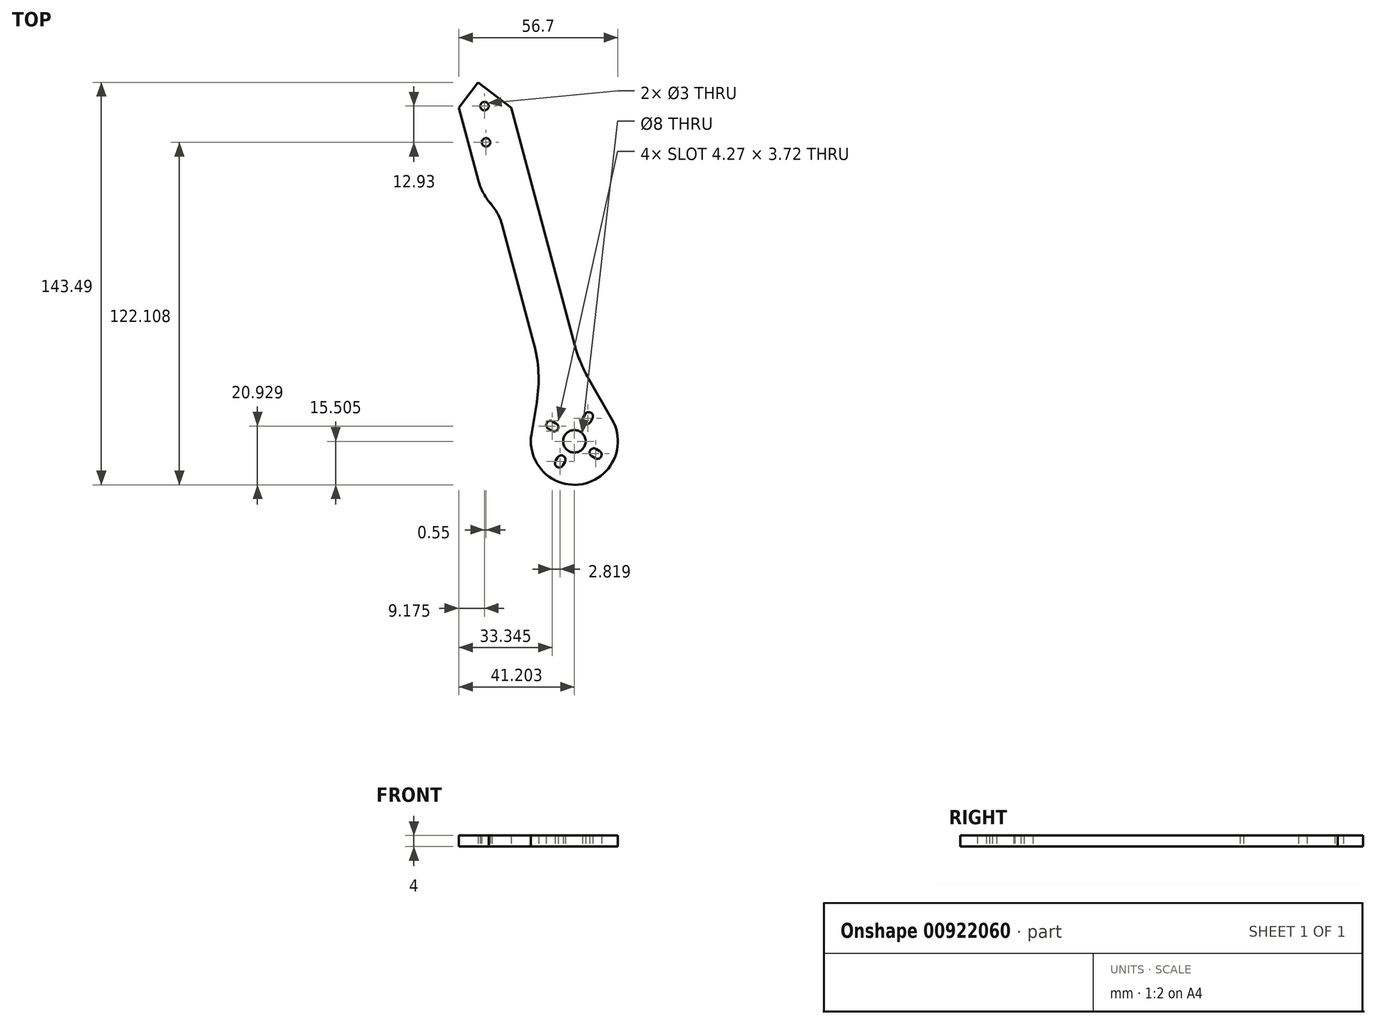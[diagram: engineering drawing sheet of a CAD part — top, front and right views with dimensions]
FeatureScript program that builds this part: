
annotation { "Feature Type Name" : "Feature", "Feature Type Description" : "" }
export const myFeature = defineFeature(function(context is Context, id is Id, definition is map)
    precondition{}
    {
        {
            var Q0;
            Q0=qCreatedBy(makeId("Top.planeOp"),FACE);
            var sketch = newSketch(context, id + "F0", { "sketchPlane" : qUnion([Q0])});
            skCircle(sketch, "E0", {"center": v(0, 0) * mm, "radius": 4 * mm});
            skLineSegment(sketch, "E1", {"start": v(0, 0) * mm, "end": v(6.19, 6.19) * mm});
            skLineSegment(sketch, "E2.bottom", {"start": v(7.78, 7.78) * mm, "end": v(7.78, 7.78) * mm});
            skLineSegment(sketch, "E2.top", {"start": v(4.6, 4.6) * mm, "end": v(4.6, 4.6) * mm});
            skLineSegment(sketch, "E2.left", {"start": v(7.78, 5.66) * mm, "end": v(6.72, 4.6) * mm});
            skLineSegment(sketch, "E2.right", {"start": v(5.66, 7.78) * mm, "end": v(4.6, 6.72) * mm});
            skPoint(sketch, "E2.middle", {"position": v(6.19, 6.19) * mm});
            skPoint(sketch, "E3.1.0", {"position": v(-6.73, 6.73) * mm});
            skLineSegment(sketch, "E3.1.1", {"start": v(-5.14, 5.14) * mm, "end": v(-5.14, 5.14) * mm});
            skLineSegment(sketch, "E3.1.2", {"start": v(-6.2, 8.32) * mm, "end": v(-5.14, 7.26) * mm});
            skLineSegment(sketch, "E3.1.3", {"start": v(-8.32, 6.2) * mm, "end": v(-7.26, 5.14) * mm});
            skLineSegment(sketch, "E3.1.4", {"start": v(-8.32, 8.32) * mm, "end": v(-8.32, 8.32) * mm});
            skPoint(sketch, "E3.2.0", {"position": v(-7.27, -6.19) * mm});
            skLineSegment(sketch, "E3.2.1", {"start": v(-5.68, -4.6) * mm, "end": v(-5.68, -4.6) * mm});
            skLineSegment(sketch, "E3.2.2", {"start": v(-8.86, -5.66) * mm, "end": v(-7.8, -4.6) * mm});
            skLineSegment(sketch, "E3.2.3", {"start": v(-6.74, -7.78) * mm, "end": v(-5.68, -6.72) * mm});
            skLineSegment(sketch, "E3.2.4", {"start": v(-8.86, -7.78) * mm, "end": v(-8.86, -7.78) * mm});
            skPoint(sketch, "E3.3.0", {"position": v(5.64, -6.73) * mm});
            skLineSegment(sketch, "E3.3.1", {"start": v(4.05, -5.14) * mm, "end": v(4.05, -5.14) * mm});
            skLineSegment(sketch, "E3.3.2", {"start": v(5.11, -8.32) * mm, "end": v(4.05, -7.26) * mm});
            skLineSegment(sketch, "E3.3.3", {"start": v(7.24, -6.2) * mm, "end": v(6.17, -5.14) * mm});
            skLineSegment(sketch, "E3.3.4", {"start": v(7.24, -8.32) * mm, "end": v(7.24, -8.32) * mm});
            skPoint(sketch, "E3.center", {"position": v(-0.54, 0) * mm});
            skPoint(sketch, "E4.visualSharp", {"position": v(-9.38, 7.26) * mm});
            skArc(sketch, "E4.filletArc", {"start": v(-8.32, 8.32) * mm, "mid": v(-8.76, 7.26) * mm, "end": v(-8.32, 6.2) * mm});
            skPoint(sketch, "E5.visualSharp", {"position": v(-7.26, 9.38) * mm});
            skArc(sketch, "E5.filletArc", {"start": v(-6.2, 8.32) * mm, "mid": v(-7.26, 8.76) * mm, "end": v(-8.32, 8.32) * mm});
            skPoint(sketch, "E6.visualSharp", {"position": v(-4.08, 6.2) * mm});
            skArc(sketch, "E6.filletArc", {"start": v(-5.14, 5.14) * mm, "mid": v(-4.7, 6.2) * mm, "end": v(-5.14, 7.26) * mm});
            skPoint(sketch, "E7.visualSharp", {"position": v(-6.2, 4.08) * mm});
            skArc(sketch, "E7.filletArc", {"start": v(-7.26, 5.14) * mm, "mid": v(-6.2, 4.7) * mm, "end": v(-5.14, 5.14) * mm});
            skPoint(sketch, "E8.visualSharp", {"position": v(6.72, 8.84) * mm});
            skArc(sketch, "E8.filletArc", {"start": v(7.78, 7.78) * mm, "mid": v(6.72, 8.22) * mm, "end": v(5.66, 7.78) * mm});
            skPoint(sketch, "E9.visualSharp", {"position": v(8.84, 6.72) * mm});
            skArc(sketch, "E9.filletArc", {"start": v(7.78, 5.66) * mm, "mid": v(8.22, 6.72) * mm, "end": v(7.78, 7.78) * mm});
            skPoint(sketch, "E10.visualSharp", {"position": v(5.66, 3.54) * mm});
            skArc(sketch, "E10.filletArc", {"start": v(4.6, 4.6) * mm, "mid": v(5.66, 4.16) * mm, "end": v(6.72, 4.6) * mm});
            skPoint(sketch, "E11.visualSharp", {"position": v(3.54, 5.66) * mm});
            skArc(sketch, "E11.filletArc", {"start": v(4.6, 6.72) * mm, "mid": v(4.16, 5.66) * mm, "end": v(4.6, 4.6) * mm});
            skPoint(sketch, "E12.visualSharp", {"position": v(5.11, -4.08) * mm});
            skArc(sketch, "E12.filletArc", {"start": v(6.17, -5.14) * mm, "mid": v(5.11, -4.7) * mm, "end": v(4.05, -5.14) * mm});
            skPoint(sketch, "E13.visualSharp", {"position": v(3, -6.2) * mm});
            skArc(sketch, "E13.filletArc", {"start": v(4.05, -5.14) * mm, "mid": v(3.61, -6.2) * mm, "end": v(4.05, -7.26) * mm});
            skPoint(sketch, "E14.visualSharp", {"position": v(6.17, -9.38) * mm});
            skArc(sketch, "E14.filletArc", {"start": v(5.11, -8.32) * mm, "mid": v(6.17, -8.76) * mm, "end": v(7.24, -8.32) * mm});
            skPoint(sketch, "E15.visualSharp", {"position": v(8.3, -7.26) * mm});
            skArc(sketch, "E15.filletArc", {"start": v(7.24, -8.32) * mm, "mid": v(7.67, -7.26) * mm, "end": v(7.24, -6.2) * mm});
            skPoint(sketch, "E16.visualSharp", {"position": v(-4.62, -5.66) * mm});
            skArc(sketch, "E16.filletArc", {"start": v(-5.68, -6.72) * mm, "mid": v(-5.24, -5.66) * mm, "end": v(-5.68, -4.6) * mm});
            skPoint(sketch, "E17.visualSharp", {"position": v(-6.74, -3.54) * mm});
            skArc(sketch, "E17.filletArc", {"start": v(-5.68, -4.6) * mm, "mid": v(-6.74, -4.16) * mm, "end": v(-7.8, -4.6) * mm});
            skPoint(sketch, "E18.visualSharp", {"position": v(-9.92, -6.72) * mm});
            skArc(sketch, "E18.filletArc", {"start": v(-8.86, -5.66) * mm, "mid": v(-9.3, -6.72) * mm, "end": v(-8.86, -7.78) * mm});
            skPoint(sketch, "E19.visualSharp", {"position": v(-7.8, -8.84) * mm});
            skArc(sketch, "E19.filletArc", {"start": v(-8.86, -7.78) * mm, "mid": v(-7.8, -8.22) * mm, "end": v(-6.74, -7.78) * mm});
            skLineSegment(sketch, "E20", {"start": v(0, 0) * mm, "end": v(-265, 0) * mm});
            skPoint(sketch, "E21.1.0", {"position": v(-270.66, -3.54) * mm});
            skPoint(sketch, "E21.1.1", {"position": v(-258.26, 3.54) * mm});
            skPoint(sketch, "E21.1.2", {"position": v(-255.08, 6.72) * mm});
            skCircle(sketch, "E21.1.3", {"center": v(-265, 0) * mm, "radius": 4 * mm});
            skPoint(sketch, "E21.1.4", {"position": v(-271.17, 9.38) * mm});
            skPoint(sketch, "E21.1.5", {"position": v(-257.2, 8.84) * mm});
            skPoint(sketch, "E21.1.6", {"position": v(-260.92, -6.2) * mm});
            skPoint(sketch, "E21.1.7", {"position": v(-270.11, 4.08) * mm});
            skPoint(sketch, "E21.1.8", {"position": v(-273.3, 7.26) * mm});
            skPoint(sketch, "E21.1.9", {"position": v(-268, 6.2) * mm});
            skPoint(sketch, "E21.1.10", {"position": v(-264.46, 0) * mm});
            skPoint(sketch, "E21.1.11", {"position": v(-271.72, -8.84) * mm});
            skPoint(sketch, "E21.1.12", {"position": v(-258.8, -4.08) * mm});
            skPoint(sketch, "E21.1.13", {"position": v(-273.84, -6.72) * mm});
            skPoint(sketch, "E21.1.14", {"position": v(-257.74, -9.38) * mm});
            skPoint(sketch, "E21.1.15", {"position": v(-268.54, -5.66) * mm});
            skPoint(sketch, "E21.1.16", {"position": v(-255.62, -7.26) * mm});
            skPoint(sketch, "E21.1.17", {"position": v(-260.38, 5.66) * mm});
            skPoint(sketch, "E21.1.18", {"position": v(-258.27, -6.73) * mm});
            skLineSegment(sketch, "E21.1.19", {"start": v(-265, 0) * mm, "end": v(-271.19, -6.19) * mm});
            skPoint(sketch, "E21.1.20", {"position": v(-271.19, -6.19) * mm});
            skPoint(sketch, "E21.1.21", {"position": v(-270.64, 6.73) * mm});
            skPoint(sketch, "E21.1.22", {"position": v(-257.73, 6.19) * mm});
            skArc(sketch, "E21.1.23", {"start": v(-271.17, 5.14) * mm, "mid": v(-270.11, 4.7) * mm, "end": v(-269.05, 5.14) * mm});
            skArc(sketch, "E21.1.24", {"start": v(-269.6, -6.72) * mm, "mid": v(-269.16, -5.66) * mm, "end": v(-269.6, -4.6) * mm});
            skArc(sketch, "E21.1.25", {"start": v(-269.6, -4.6) * mm, "mid": v(-270.66, -4.16) * mm, "end": v(-271.72, -4.6) * mm});
            skArc(sketch, "E21.1.26", {"start": v(-256.68, -8.32) * mm, "mid": v(-256.24, -7.26) * mm, "end": v(-256.68, -6.2) * mm});
            skArc(sketch, "E21.1.27", {"start": v(-258.8, -8.32) * mm, "mid": v(-257.74, -8.76) * mm, "end": v(-256.68, -8.32) * mm});
            skLineSegment(sketch, "E21.1.28", {"start": v(-258.8, -8.32) * mm, "end": v(-259.86, -7.26) * mm});
            skArc(sketch, "E21.1.29", {"start": v(-257.74, -5.14) * mm, "mid": v(-258.8, -4.7) * mm, "end": v(-259.86, -5.14) * mm});
            skArc(sketch, "E21.1.30", {"start": v(-259.86, -5.14) * mm, "mid": v(-260.3, -6.2) * mm, "end": v(-259.86, -7.26) * mm});
            skLineSegment(sketch, "E21.1.31", {"start": v(-256.68, -6.2) * mm, "end": v(-257.74, -5.14) * mm});
            skArc(sketch, "E21.1.32", {"start": v(-256.14, 7.78) * mm, "mid": v(-257.2, 8.22) * mm, "end": v(-258.26, 7.78) * mm});
            skLineSegment(sketch, "E21.1.33", {"start": v(-270.11, 8.32) * mm, "end": v(-269.05, 7.26) * mm});
            skArc(sketch, "E21.1.34", {"start": v(-272.78, -5.66) * mm, "mid": v(-273.22, -6.72) * mm, "end": v(-272.78, -7.78) * mm});
            skLineSegment(sketch, "E21.1.35", {"start": v(-272.24, 6.2) * mm, "end": v(-271.17, 5.14) * mm});
            skArc(sketch, "E21.1.36", {"start": v(-270.11, 8.32) * mm, "mid": v(-271.17, 8.76) * mm, "end": v(-272.24, 8.32) * mm});
            skArc(sketch, "E21.1.37", {"start": v(-259.32, 4.6) * mm, "mid": v(-258.26, 4.16) * mm, "end": v(-257.2, 4.6) * mm});
            skArc(sketch, "E21.1.38", {"start": v(-259.32, 6.72) * mm, "mid": v(-259.76, 5.66) * mm, "end": v(-259.32, 4.6) * mm});
            skLineSegment(sketch, "E21.1.39", {"start": v(-256.14, 5.66) * mm, "end": v(-257.2, 4.6) * mm});
            skArc(sketch, "E21.1.40", {"start": v(-269.05, 5.14) * mm, "mid": v(-268.61, 6.2) * mm, "end": v(-269.05, 7.26) * mm});
            skArc(sketch, "E21.1.41", {"start": v(-272.24, 8.32) * mm, "mid": v(-272.67, 7.26) * mm, "end": v(-272.24, 6.2) * mm});
            skArc(sketch, "E21.1.42", {"start": v(-256.14, 5.66) * mm, "mid": v(-255.7, 6.72) * mm, "end": v(-256.14, 7.78) * mm});
            skLineSegment(sketch, "E21.1.43", {"start": v(-258.26, 7.78) * mm, "end": v(-259.32, 6.72) * mm});
            skArc(sketch, "E21.1.44", {"start": v(-272.78, -7.78) * mm, "mid": v(-271.72, -8.22) * mm, "end": v(-270.66, -7.78) * mm});
            skLineSegment(sketch, "E21.1.45", {"start": v(-270.66, -7.78) * mm, "end": v(-269.6, -6.72) * mm});
            skLineSegment(sketch, "E21.1.46", {"start": v(-272.78, -5.66) * mm, "end": v(-271.72, -4.6) * mm});
            skPoint(sketch, "E21.center", {"position": v(-132.5, 0) * mm});
            skPoint(sketch, "E22.1.0", {"position": v(-161.58, 132.48) * mm});
            skPoint(sketch, "E22.1.1", {"position": v(-169.13, 120.94) * mm});
            skLineSegment(sketch, "E22.1.2", {"start": v(-166.8, 127.99) * mm, "end": v(-174.37, 132.36) * mm});
            skPoint(sketch, "E22.1.3", {"position": v(-174.37, 132.36) * mm});
            skPoint(sketch, "E22.1.4", {"position": v(-157.74, 120.14) * mm});
            skPoint(sketch, "E22.1.5", {"position": v(-166.65, 127.46) * mm});
            skPoint(sketch, "E22.1.6", {"position": v(-177.07, 132.19) * mm});
            skPoint(sketch, "E22.1.7", {"position": v(-156.24, 122.74) * mm});
            skPoint(sketch, "E22.1.8", {"position": v(-175.57, 134.78) * mm});
            skPoint(sketch, "E22.1.9", {"position": v(-160.13, 124.99) * mm});
            skPoint(sketch, "E22.1.10", {"position": v(-164.18, 133.98) * mm});
            skPoint(sketch, "E22.1.11", {"position": v(-158.93, 122.56) * mm});
            skPoint(sketch, "E22.1.12", {"position": v(-171.73, 122.44) * mm});
            skPoint(sketch, "E22.1.13", {"position": v(-161.63, 122.39) * mm});
            skPoint(sketch, "E22.1.14", {"position": v(-171.55, 119.74) * mm});
            skPoint(sketch, "E22.1.15", {"position": v(-173.98, 118.54) * mm});
            skPoint(sketch, "E22.1.16", {"position": v(-159.33, 136.38) * mm});
            skPoint(sketch, "E22.1.17", {"position": v(-161.93, 137.88) * mm});
            skCircle(sketch, "E22.1.18", {"center": v(-166.8, 127.99) * mm, "radius": 4 * mm});
            skPoint(sketch, "E22.1.19", {"position": v(-161.75, 135.18) * mm});
            skPoint(sketch, "E22.1.20", {"position": v(-171.67, 132.53) * mm});
            skPoint(sketch, "E22.1.21", {"position": v(-173.17, 129.94) * mm});
            skPoint(sketch, "E22.1.22", {"position": v(-171.38, 117.04) * mm});
            skArc(sketch, "E22.1.23", {"start": v(-156.99, 121.44) * mm, "mid": v(-156.84, 122.57) * mm, "end": v(-157.54, 123.49) * mm});
            skArc(sketch, "E22.1.24", {"start": v(-176.32, 133.49) * mm, "mid": v(-176.47, 132.35) * mm, "end": v(-175.77, 131.44) * mm});
            skArc(sketch, "E22.1.25", {"start": v(-174.47, 130.69) * mm, "mid": v(-173.33, 130.54) * mm, "end": v(-172.42, 131.24) * mm});
            skArc(sketch, "E22.1.26", {"start": v(-169.88, 119.64) * mm, "mid": v(-169.73, 120.78) * mm, "end": v(-170.43, 121.7) * mm});
            skArc(sketch, "E22.1.27", {"start": v(-172.42, 131.24) * mm, "mid": v(-172.27, 132.37) * mm, "end": v(-172.97, 133.28) * mm});
            skLineSegment(sketch, "E22.1.28", {"start": v(-174.27, 134.03) * mm, "end": v(-172.97, 133.28) * mm});
            skLineSegment(sketch, "E22.1.29", {"start": v(-170.63, 118.34) * mm, "end": v(-169.88, 119.64) * mm});
            skArc(sketch, "E22.1.30", {"start": v(-170.43, 121.7) * mm, "mid": v(-171.57, 121.84) * mm, "end": v(-172.48, 121.14) * mm});
            skLineSegment(sketch, "E22.1.31", {"start": v(-162.68, 136.58) * mm, "end": v(-163.43, 135.28) * mm});
            skLineSegment(sketch, "E22.1.32", {"start": v(-159.04, 120.89) * mm, "end": v(-160.33, 121.64) * mm});
            skLineSegment(sketch, "E22.1.33", {"start": v(-175.77, 131.44) * mm, "end": v(-174.47, 130.69) * mm});
            skArc(sketch, "E22.1.34", {"start": v(-160.63, 137.13) * mm, "mid": v(-161.77, 137.28) * mm, "end": v(-162.68, 136.58) * mm});
            skArc(sketch, "E22.1.35", {"start": v(-159.04, 120.89) * mm, "mid": v(-157.9, 120.74) * mm, "end": v(-156.99, 121.44) * mm});
            skLineSegment(sketch, "E22.1.36", {"start": v(-160.08, 135.08) * mm, "end": v(-160.83, 133.78) * mm});
            skArc(sketch, "E22.1.37", {"start": v(-172.68, 117.8) * mm, "mid": v(-171.54, 117.64) * mm, "end": v(-170.63, 118.34) * mm});
            skArc(sketch, "E22.1.38", {"start": v(-163.43, 135.28) * mm, "mid": v(-163.58, 134.14) * mm, "end": v(-162.88, 133.23) * mm});
            skArc(sketch, "E22.1.39", {"start": v(-162.88, 133.23) * mm, "mid": v(-161.74, 133.08) * mm, "end": v(-160.83, 133.78) * mm});
            skLineSegment(sketch, "E22.1.40", {"start": v(-173.23, 119.84) * mm, "end": v(-172.48, 121.14) * mm});
            skArc(sketch, "E22.1.41", {"start": v(-160.08, 135.08) * mm, "mid": v(-159.93, 136.22) * mm, "end": v(-160.63, 137.13) * mm});
            skArc(sketch, "E22.1.42", {"start": v(-158.83, 124.24) * mm, "mid": v(-159.97, 124.39) * mm, "end": v(-160.88, 123.69) * mm});
            skLineSegment(sketch, "E22.1.43", {"start": v(-157.54, 123.49) * mm, "end": v(-158.83, 124.24) * mm});
            skArc(sketch, "E22.1.44", {"start": v(-174.27, 134.03) * mm, "mid": v(-175.4, 134.18) * mm, "end": v(-176.32, 133.49) * mm});
            skArc(sketch, "E22.1.45", {"start": v(-173.23, 119.84) * mm, "mid": v(-173.38, 118.7) * mm, "end": v(-172.68, 117.8) * mm});
            skArc(sketch, "E22.1.46", {"start": v(-160.88, 123.69) * mm, "mid": v(-161.03, 122.55) * mm, "end": v(-160.33, 121.64) * mm});
            skLineSegment(sketch, "E22.anchor1", {"start": v(-132.5, 0) * mm, "end": v(-265, 0) * mm, "construction": true});
            skLineSegment(sketch, "E22.anchor2", {"start": v(-132.5, 0) * mm, "end": v(-166.8, 127.99) * mm, "construction": true});
            skPoint(sketch, "E23.1.0", {"position": v(-103.07, -137.88) * mm});
            skPoint(sketch, "E23.1.1", {"position": v(-90.63, -132.36) * mm});
            skPoint(sketch, "E23.1.2", {"position": v(-93.33, -132.53) * mm});
            skPoint(sketch, "E23.1.3", {"position": v(-108.76, -122.74) * mm});
            skPoint(sketch, "E23.1.4", {"position": v(-87.93, -132.19) * mm});
            skPoint(sketch, "E23.1.5", {"position": v(-103.25, -135.18) * mm});
            skPoint(sketch, "E23.1.6", {"position": v(-104.87, -124.99) * mm});
            skPoint(sketch, "E23.1.7", {"position": v(-103.37, -122.39) * mm});
            skPoint(sketch, "E23.1.8", {"position": v(-93.27, -122.44) * mm});
            skPoint(sketch, "E23.1.9", {"position": v(-95.87, -120.94) * mm});
            skPoint(sketch, "E23.1.10", {"position": v(-103.42, -132.48) * mm});
            skCircle(sketch, "E23.1.11", {"center": v(-98.2, -127.99) * mm, "radius": 4 * mm});
            skPoint(sketch, "E23.1.12", {"position": v(-106.07, -122.56) * mm});
            skPoint(sketch, "E23.1.13", {"position": v(-107.26, -120.14) * mm});
            skPoint(sketch, "E23.1.14", {"position": v(-93.45, -119.74) * mm});
            skLineSegment(sketch, "E23.1.15", {"start": v(-98.2, -127.99) * mm, "end": v(-90.63, -132.36) * mm});
            skPoint(sketch, "E23.1.16", {"position": v(-91.02, -118.54) * mm});
            skPoint(sketch, "E23.1.17", {"position": v(-93.62, -117.04) * mm});
            skPoint(sketch, "E23.1.18", {"position": v(-100.82, -133.98) * mm});
            skPoint(sketch, "E23.1.19", {"position": v(-105.67, -136.38) * mm});
            skPoint(sketch, "E23.1.20", {"position": v(-91.83, -129.94) * mm});
            skPoint(sketch, "E23.1.21", {"position": v(-98.35, -127.46) * mm});
            skPoint(sketch, "E23.1.22", {"position": v(-89.43, -134.78) * mm});
            skArc(sketch, "E23.1.23", {"start": v(-102.12, -133.23) * mm, "mid": v(-103.26, -133.08) * mm, "end": v(-104.17, -133.78) * mm});
            skArc(sketch, "E23.1.24", {"start": v(-92.58, -131.24) * mm, "mid": v(-92.73, -132.37) * mm, "end": v(-92.03, -133.28) * mm});
            skArc(sketch, "E23.1.25", {"start": v(-104.92, -135.08) * mm, "mid": v(-105.07, -136.22) * mm, "end": v(-104.37, -137.13) * mm});
            skArc(sketch, "E23.1.26", {"start": v(-106.17, -124.24) * mm, "mid": v(-105.03, -124.39) * mm, "end": v(-104.12, -123.69) * mm});
            skLineSegment(sketch, "E23.1.27", {"start": v(-107.46, -123.49) * mm, "end": v(-106.17, -124.24) * mm});
            skArc(sketch, "E23.1.28", {"start": v(-90.53, -130.69) * mm, "mid": v(-91.67, -130.54) * mm, "end": v(-92.58, -131.24) * mm});
            skArc(sketch, "E23.1.29", {"start": v(-101.57, -135.28) * mm, "mid": v(-101.42, -134.14) * mm, "end": v(-102.12, -133.23) * mm});
            skArc(sketch, "E23.1.30", {"start": v(-104.37, -137.13) * mm, "mid": v(-103.23, -137.28) * mm, "end": v(-102.32, -136.58) * mm});
            skLineSegment(sketch, "E23.1.31", {"start": v(-91.77, -119.84) * mm, "end": v(-92.52, -121.14) * mm});
            skArc(sketch, "E23.1.32", {"start": v(-105.96, -120.89) * mm, "mid": v(-107.1, -120.74) * mm, "end": v(-108.01, -121.44) * mm});
            skArc(sketch, "E23.1.33", {"start": v(-95.12, -119.64) * mm, "mid": v(-95.27, -120.78) * mm, "end": v(-94.57, -121.7) * mm});
            skLineSegment(sketch, "E23.1.34", {"start": v(-94.37, -118.34) * mm, "end": v(-95.12, -119.64) * mm});
            skLineSegment(sketch, "E23.1.35", {"start": v(-105.96, -120.89) * mm, "end": v(-104.67, -121.64) * mm});
            skArc(sketch, "E23.1.36", {"start": v(-91.77, -119.84) * mm, "mid": v(-91.62, -118.7) * mm, "end": v(-92.32, -117.8) * mm});
            skArc(sketch, "E23.1.37", {"start": v(-88.68, -133.49) * mm, "mid": v(-88.53, -132.35) * mm, "end": v(-89.23, -131.44) * mm});
            skArc(sketch, "E23.1.38", {"start": v(-90.73, -134.03) * mm, "mid": v(-89.6, -134.18) * mm, "end": v(-88.68, -133.49) * mm});
            skLineSegment(sketch, "E23.1.39", {"start": v(-104.92, -135.08) * mm, "end": v(-104.17, -133.78) * mm});
            skLineSegment(sketch, "E23.1.40", {"start": v(-89.23, -131.44) * mm, "end": v(-90.53, -130.69) * mm});
            skLineSegment(sketch, "E23.1.41", {"start": v(-102.32, -136.58) * mm, "end": v(-101.57, -135.28) * mm});
            skArc(sketch, "E23.1.42", {"start": v(-92.32, -117.8) * mm, "mid": v(-93.46, -117.64) * mm, "end": v(-94.37, -118.34) * mm});
            skArc(sketch, "E23.1.43", {"start": v(-108.01, -121.44) * mm, "mid": v(-108.16, -122.57) * mm, "end": v(-107.46, -123.49) * mm});
            skLineSegment(sketch, "E23.1.44", {"start": v(-90.73, -134.03) * mm, "end": v(-92.03, -133.28) * mm});
            skArc(sketch, "E23.1.45", {"start": v(-104.12, -123.69) * mm, "mid": v(-103.97, -122.55) * mm, "end": v(-104.67, -121.64) * mm});
            skArc(sketch, "E23.1.46", {"start": v(-94.57, -121.7) * mm, "mid": v(-93.43, -121.84) * mm, "end": v(-92.52, -121.14) * mm});
            skLineSegment(sketch, "E23.anchor1", {"start": v(-132.5, 0) * mm, "end": v(-166.65, 127.46) * mm, "construction": true});
            skLineSegment(sketch, "E23.anchor2", {"start": v(-132.5, 0) * mm, "end": v(-98.35, -127.46) * mm, "construction": true});
            skSolve(sketch);
        }
        {
            var Q0;
            Q0=qCreatedBy(makeId("Top.planeOp"),FACE);
            var sketch = newSketch(context, id + "F1", { "sketchPlane" : qUnion([Q0])});
            skCircle(sketch, "E24", {"center": v(-123.75, 0) * mm, "radius": 1.5 * mm});
            skCircle(sketch, "E25", {"center": v(-102.5, 0) * mm, "radius": 1.5 * mm});
            skLineSegment(sketch, "E26", {"start": v(-98.2, -127.99) * mm, "end": v(-166.8, 127.99) * mm});
            skLineSegment(sketch, "E27", {"start": v(-265, 0) * mm, "end": v(0, 0) * mm});
            skCircle(sketch, "E28", {"center": v(-162.5, 0) * mm, "radius": 1.5 * mm});
            skCircle(sketch, "E29", {"center": v(-141.25, 0) * mm, "radius": 1.5 * mm});
            skCircle(sketch, "E30", {"center": v(-130.24, -8.45) * mm, "radius": 1.5 * mm});
            skCircle(sketch, "E31", {"center": v(-124.74, -28.98) * mm, "radius": 1.5 * mm});
            skCircle(sketch, "E32", {"center": v(-140.26, 28.98) * mm, "radius": 1.5 * mm});
            skCircle(sketch, "E33", {"center": v(-134.76, 8.45) * mm, "radius": 1.5 * mm});
            skSolve(sketch);
        }
        {
            var Q0;
            Q0=qCreatedBy(makeId("Top.planeOp"),FACE);
            var sketch = newSketch(context, id + "F2", { "sketchPlane" : qUnion([Q0])});
            skLineSegment(sketch, "E34", {"start": v(-141.25, 0) * mm, "end": v(-130.24, -8.45) * mm, "construction": true});
            skLineSegment(sketch, "E35", {"start": v(-130.24, -8.45) * mm, "end": v(-123.75, 0) * mm, "construction": true});
            skLineSegment(sketch, "E36", {"start": v(-123.75, 0) * mm, "end": v(-134.76, 8.45) * mm, "construction": true});
            skLineSegment(sketch, "E37", {"start": v(-134.76, 8.45) * mm, "end": v(-141.25, 0) * mm, "construction": true});
            skLineSegment(sketch, "E38", {"start": v(-153.88, -2.82) * mm, "end": v(-129.68, -21.38) * mm, "construction": true});
            skLineSegment(sketch, "E39", {"start": v(-129.68, -21.38) * mm, "end": v(-111.12, 2.82) * mm, "construction": true});
            skLineSegment(sketch, "E40", {"start": v(-111.12, 2.82) * mm, "end": v(-135.32, 21.38) * mm, "construction": true});
            skLineSegment(sketch, "E41", {"start": v(-135.32, 21.38) * mm, "end": v(-153.88, -2.82) * mm, "construction": true});
            skLineSegment(sketch, "E42", {"start": v(-153.88, -2.82) * mm, "end": v(-111.12, 2.82) * mm, "construction": true});
            skLineSegment(sketch, "E43", {"start": v(-135.32, 21.38) * mm, "end": v(-129.68, -21.38) * mm, "construction": true});
            skCircle(sketch, "E44", {"center": v(-135.32, 21.38) * mm, "radius": 1.5 * mm});
            skCircle(sketch, "E45", {"center": v(-153.88, -2.82) * mm, "radius": 1.5 * mm});
            skCircle(sketch, "E46", {"center": v(-129.68, -21.38) * mm, "radius": 1.5 * mm});
            skCircle(sketch, "E47", {"center": v(-111.12, 2.82) * mm, "radius": 1.5 * mm});
            skSolve(sketch);
        }
        {
            var Q0;
            Q0=qCreatedBy(makeId("Top.planeOp"),FACE);
            var sketch = newSketch(context, id + "F3", { "sketchPlane" : qUnion([Q0])});
            skLineSegment(sketch, "E48", {"start": v(-132.5, 0) * mm, "end": v(-138, 4.23) * mm});
            skLineSegment(sketch, "E49", {"start": v(-132.5, 0) * mm, "end": v(-129.26, 4.23) * mm});
            skLineSegment(sketch, "E50", {"start": v(-132.5, 0) * mm, "end": v(-127, -4.23) * mm});
            skLineSegment(sketch, "E51", {"start": v(-132.5, 0) * mm, "end": v(-135.74, -4.23) * mm});
            skCircle(sketch, "E52", {"center": v(-265, 0) * mm, "radius": 15.5 * mm});
            skCircle(sketch, "E53", {"center": v(-166.8, 127.99) * mm, "radius": 15.5 * mm});
            skCircle(sketch, "E54", {"center": v(0, 0) * mm, "radius": 15.5 * mm});
            skCircle(sketch, "E55", {"center": v(-98.2, -127.99) * mm, "radius": 15.5 * mm});
            skLineSegment(sketch, "E56", {"start": v(-144.23, 9) * mm, "end": v(-238.23, 9) * mm});
            skLineSegment(sketch, "E57", {"start": v(-138, 4.23) * mm, "end": v(-144.23, 9) * mm});
            skLineSegment(sketch, "E58", {"start": v(-144.23, 9) * mm, "end": v(-168.56, 99.8) * mm});
            skLineSegment(sketch, "E59", {"start": v(-127, -4.23) * mm, "end": v(-120.77, -9) * mm});
            skLineSegment(sketch, "E60", {"start": v(-120.77, -9) * mm, "end": v(-26.77, -9) * mm});
            skLineSegment(sketch, "E61", {"start": v(-120.77, -9) * mm, "end": v(-98.11, -93.57) * mm});
            skLineSegment(sketch, "E62", {"start": v(-93.25, -105.4) * mm, "end": v(-84.74, -120.3) * mm});
            skLineSegment(sketch, "E63", {"start": v(-132.43, -35.03) * mm, "end": v(-139.4, -9) * mm});
            skLineSegment(sketch, "E64", {"start": v(-135.74, -4.23) * mm, "end": v(-139.4, -9) * mm});
            skLineSegment(sketch, "E65", {"start": v(-96.44, -99.8) * mm, "end": v(-109.85, -103.39) * mm});
            skPoint(sketch, "E66.visualSharp", {"position": v(-96.44, -99.8) * mm});
            skArc(sketch, "E66.filletArc", {"start": v(-98.11, -93.57) * mm, "mid": v(-96.06, -99.64) * mm, "end": v(-93.25, -105.4) * mm});
            skLineSegment(sketch, "E67", {"start": v(-112.65, -92.95) * mm, "end": v(-123.85, -51.12) * mm});
            skLineSegment(sketch, "E68", {"start": v(-111.61, -114.05) * mm, "end": v(-113.5, -125.46) * mm});
            skLineSegment(sketch, "E69", {"start": v(-127.53, -43.71) * mm, "end": v(-128.75, -42.44) * mm});
            skPoint(sketch, "E70.visualSharp", {"position": v(-109.85, -103.39) * mm});
            skArc(sketch, "E70.filletArc", {"start": v(-111.61, -114.05) * mm, "mid": v(-111, -103.45) * mm, "end": v(-112.65, -92.95) * mm});
            skPoint(sketch, "E71.visualSharp", {"position": v(-125.18, -46.15) * mm});
            skArc(sketch, "E71.filletArc", {"start": v(-123.85, -51.12) * mm, "mid": v(-125.75, -46.47) * mm, "end": v(-128.75, -42.44) * mm});
            skPoint(sketch, "E72.visualSharp", {"position": v(-131.1, -40) * mm});
            skArc(sketch, "E72.filletArc", {"start": v(-132.43, -35.03) * mm, "mid": v(-130.53, -39.68) * mm, "end": v(-127.53, -43.71) * mm});
            skSolve(sketch);
        }
        {
            var Q0;
            Q0=makeQuery(id+"F3.imprint","IMPRINT",FACE,{"disambiguationData":[TD([[makeQuery(id+"F3.imprint","IMPRINT",EDGE,{"derivedFrom":sQuery(id+"F3.wireOp",EDGE,"E50")}),-1.0]])]});
            var Q1;
            {var subQ0=sQuery(id+"F3.wireOp",EDGE,"E55");var subQ1=makeQuery(id+"F3.imprint","INTERSECT",VERTEX,{"derivedFrom":[subQ0,sQuery(id+"F3.wireOp",EDGE,"E62")]});Q1=makeQuery(id+"F3.imprint","IMPRINT",FACE,{"disambiguationData":[TD([[makeQuery(id+"F3.imprint","IMPRINT",EDGE,{"disambiguationData":[TD([[subQ1,-1.0]])],"derivedFrom":subQ0}),1.0]])]});}
            extrude(context, id + "F4", {"entities" : qUnion([Q0, Q1]), "depth" : 4 * mm, "offsetDistance" : 25 * mm});
        }
        {
            var Q0;
            Q0=makeQuery(id+"F0.imprint","IMPRINT",FACE,{"disambiguationData":[TD([[makeQuery(id+"F0.imprint","IMPRINT",EDGE,{"derivedFrom":sQuery(id+"F0.wireOp",EDGE,"E23.1.23")}),1.0]])]});
            var Q1;
            Q1=makeQuery(id+"F0.imprint","IMPRINT",FACE,{"disambiguationData":[TD([[makeQuery(id+"F0.imprint","IMPRINT",EDGE,{"derivedFrom":sQuery(id+"F0.wireOp",EDGE,"E23.1.11")}),1.0]])]});
            var Q2;
            Q2=makeQuery(id+"F0.imprint","IMPRINT",FACE,{"disambiguationData":[TD([[makeQuery(id+"F0.imprint","IMPRINT",EDGE,{"derivedFrom":sQuery(id+"F0.wireOp",EDGE,"E23.1.26")}),1.0]])]});
            var Q3;
            Q3=makeQuery(id+"F0.imprint","IMPRINT",FACE,{"disambiguationData":[TD([[makeQuery(id+"F0.imprint","IMPRINT",EDGE,{"derivedFrom":sQuery(id+"F0.wireOp",EDGE,"E23.1.31")}),-1.0]])]});
            var Q4;
            Q4=makeQuery(id+"F0.imprint","IMPRINT",FACE,{"disambiguationData":[TD([[makeQuery(id+"F0.imprint","IMPRINT",EDGE,{"derivedFrom":sQuery(id+"F0.wireOp",EDGE,"E23.1.24")}),1.0]])]});
            var Q5;
            {var subQ0=sQuery(id+"F1.wireOp",EDGE,"E31");var subQ1=sQuery(id+"F1.wireOp",EDGE,"E26");var subQ2=makeQuery(id+"F1.imprint","INTERSECT",VERTEX,{"disambiguationData":[OD(0.0)],"derivedFrom":[subQ1,subQ0]});Q5=makeQuery(id+"F1.imprint","IMPRINT",FACE,{"disambiguationData":[TD([[makeQuery(id+"F1.imprint","IMPRINT",EDGE,{"disambiguationData":[TD([[subQ2,-1.0]])],"derivedFrom":subQ1}),-1.0]])]});}
            var Q6;
            {var subQ0=sQuery(id+"F1.wireOp",EDGE,"E31");var subQ1=sQuery(id+"F1.wireOp",EDGE,"E26");var subQ2=makeQuery(id+"F1.imprint","INTERSECT",VERTEX,{"disambiguationData":[OD(0.0)],"derivedFrom":[subQ1,subQ0]});Q6=makeQuery(id+"F1.imprint","IMPRINT",FACE,{"disambiguationData":[TD([[makeQuery(id+"F1.imprint","IMPRINT",EDGE,{"disambiguationData":[TD([[subQ2,-1.0]])],"derivedFrom":subQ1}),1.0]])]});}
            var Q7;
            Q7=makeQuery(id+"F2.imprint","IMPRINT",FACE,{"disambiguationData":[TD([[makeQuery(id+"F2.imprint","IMPRINT",EDGE,{"derivedFrom":sQuery(id+"F2.wireOp",EDGE,"E46")}),1.0]])]});
            var Q8;
            {var subQ0=sQuery(id+"F1.wireOp",EDGE,"E30");var subQ1=sQuery(id+"F1.wireOp",EDGE,"E26");var subQ2=makeQuery(id+"F1.imprint","INTERSECT",VERTEX,{"disambiguationData":[OD(0.0)],"derivedFrom":[subQ1,subQ0]});Q8=makeQuery(id+"F1.imprint","IMPRINT",FACE,{"disambiguationData":[TD([[makeQuery(id+"F1.imprint","IMPRINT",EDGE,{"disambiguationData":[TD([[subQ2,-1.0]])],"derivedFrom":subQ1}),-1.0]])]});}
            var Q9;
            {var subQ0=sQuery(id+"F1.wireOp",EDGE,"E30");var subQ1=sQuery(id+"F1.wireOp",EDGE,"E26");var subQ2=makeQuery(id+"F1.imprint","INTERSECT",VERTEX,{"disambiguationData":[OD(0.0)],"derivedFrom":[subQ1,subQ0]});Q9=makeQuery(id+"F1.imprint","IMPRINT",FACE,{"disambiguationData":[TD([[makeQuery(id+"F1.imprint","IMPRINT",EDGE,{"disambiguationData":[TD([[subQ2,-1.0]])],"derivedFrom":subQ1}),1.0]])]});}
            extrude(context, id + "F5", {"entities" : qUnion([Q0, Q1, Q2, Q3, Q4, Q5, Q6, Q7, Q8, Q9]), "operationType" : NewBodyOperationType.REMOVE, "depth" : 25 * mm, "offsetDistance" : 25 * mm});
        }
    });
